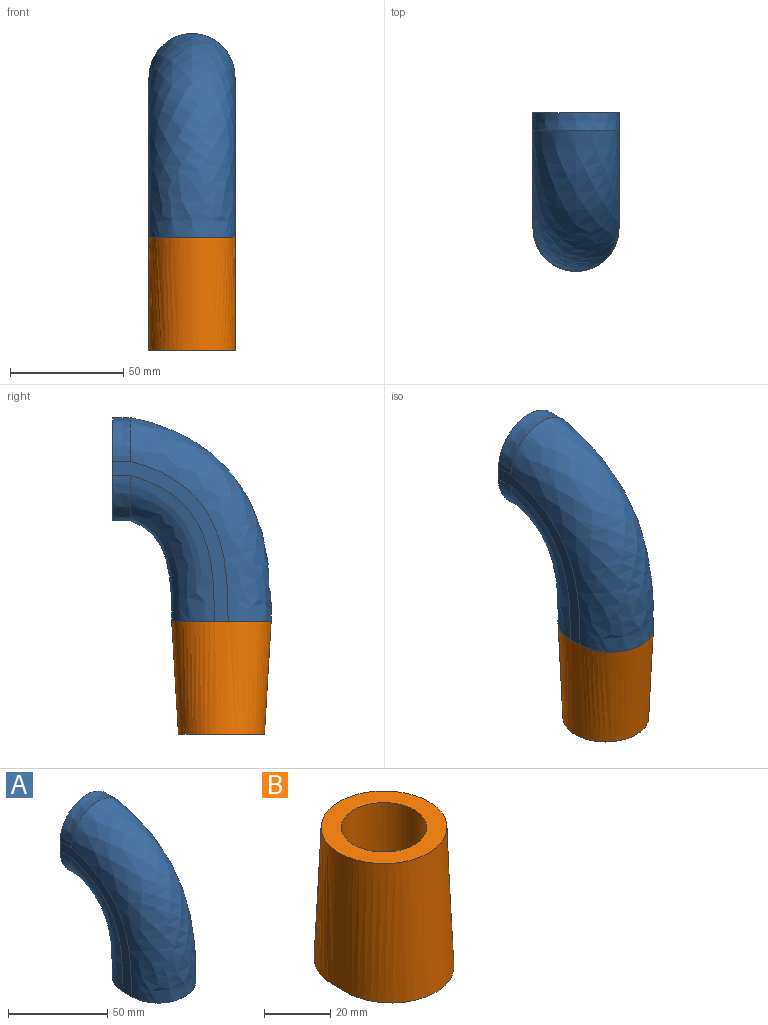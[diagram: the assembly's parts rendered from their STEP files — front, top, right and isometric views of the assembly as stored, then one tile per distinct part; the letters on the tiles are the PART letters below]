
ASSEMBLY  parts=2 mates=1
PART A: 12 faces, bbox 43.4x105.4x116.2 mm
  f0: plane 49.39x43.39mm, normal (0,0,-1), area 839.3mm2, adj f1,f2,f3,f4,f5
  f1: bspline ~110.81x95.75mm, area 6397.5mm2, adj f0,f2,f4,f7
  f2: plane 71.67x52.15mm, normal (1,0,0), area 579.1mm2, adj f0,f1,f3,f7,f8,f9
  f3: bspline ~67.01x55.99mm, area 3930.4mm2, adj f0,f2,f4,f8
  f4: plane 72.33x52.15mm, normal (-1,0,0), area 578.8mm2, adj f0,f1,f3,f7,f8,f9
  f5: cylinder r=12.9mm len=40mm, axis (0,0,-1), area 3242.1mm2, adj f0,f6
  f6: plane 25.8x25.8mm, normal (0,0,-1), area 522.8mm2, adj f5
  f7: extruded ~38x19.47mm, area 483.8mm2, adj f1,f2,f4,f9
  f8: extruded ~38x19.95mm, area 489.1mm2, adj f2,f3,f4,f9
  f9: plane 45.65x38.02mm, normal (0,1,0), area 888.3mm2, adj f2,f4,f7,f8,f11
  f10: plane 25.8x25.8mm, normal (0,1,0), area 522.8mm2, adj f11
  f11: cylinder r=12.9mm len=25.8mm, axis (0,1,0), area 1864.2mm2, adj f9,f10
PART B: 4 faces, bbox 39.6x45.6x51.6 mm
  f0: plane 44.19x38.19mm, normal (0,0,-1), area 839.3mm2, adj f2,f3
  f1: plane 39.56x39.56mm, normal (0,0,1), area 611.3mm2, adj f2,f3
  f2: bspline ~50x43.97mm, area 6252.3mm2, adj f0,f1
  f3: cylinder r=12.9mm len=50mm, axis (0,0,-1), area 4052.7mm2, adj f0,f1
PLACE A at identity
PLACE B rot(axis=(1,0,0),180deg) t=(0,0,0)mm
MATE fastened B.f3 <-> A.f5  axis (0,0,1) through (0,0,0)mm
